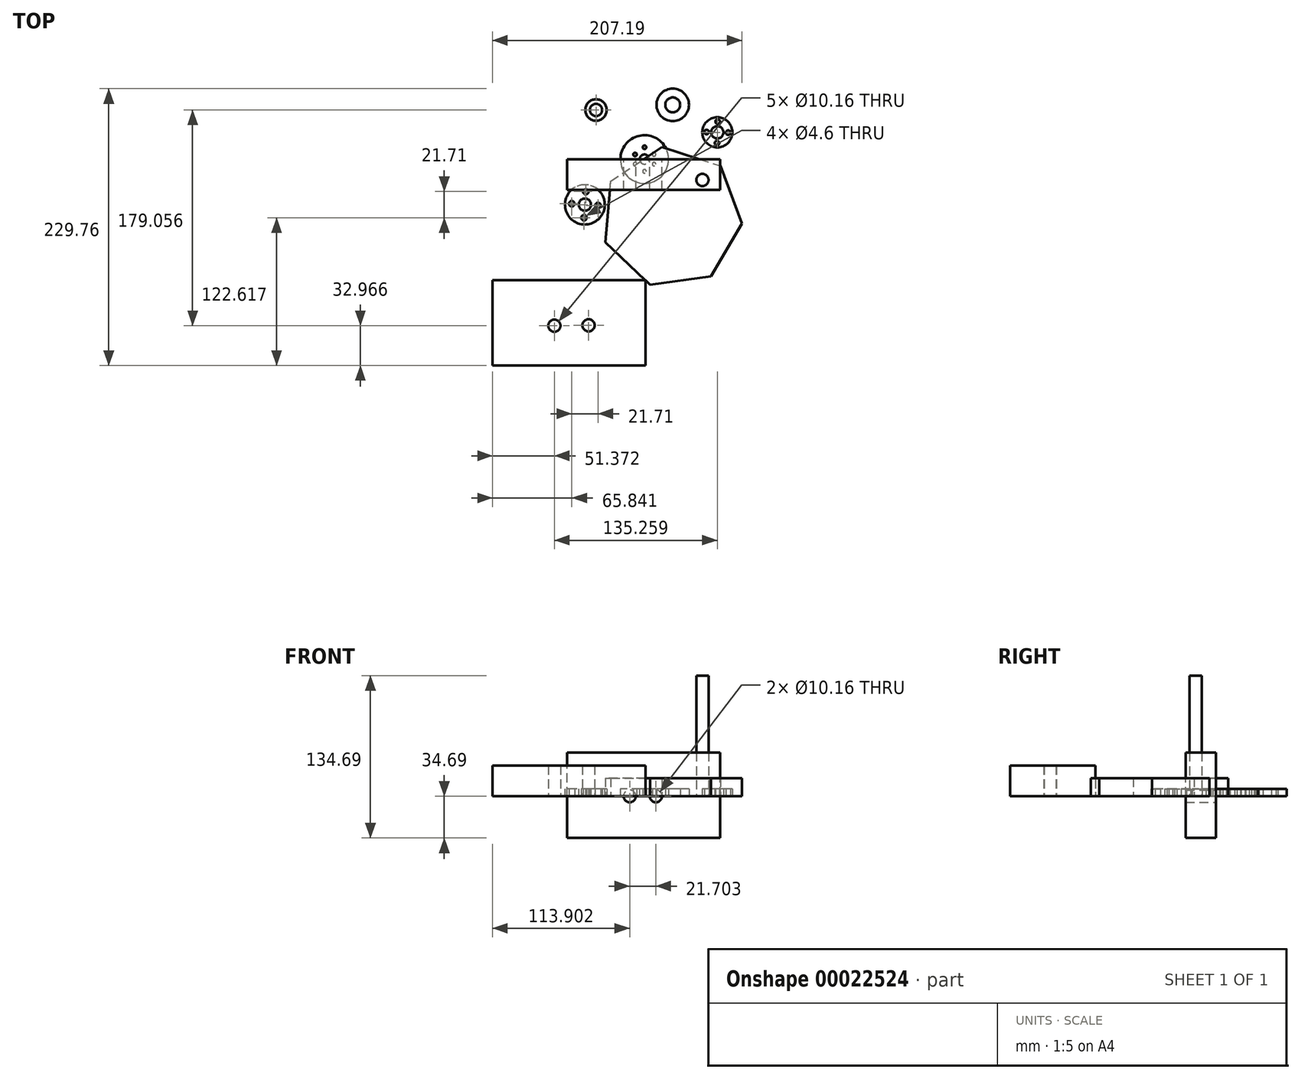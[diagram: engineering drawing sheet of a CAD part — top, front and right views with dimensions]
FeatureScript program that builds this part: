
annotation { "Feature Type Name" : "Feature", "Feature Type Description" : "" }
export const myFeature = defineFeature(function(context is Context, id is Id, definition is map)
    precondition{}
    {
        {
            var Q0;
            Q0=qCreatedBy(makeId("Top.planeOp"),FACE);
            var sketch = newSketch(context, id + "F0", { "sketchPlane" : qUnion([Q0])});
            skArc(sketch, "E0", {"start": v(20, 0) * mm, "mid": v(0, 20) * mm, "end": v(-20, 0) * mm});
            skLineSegment(sketch, "E1", {"start": v(-20, 0) * mm, "end": v(20, 0) * mm});
            skLineSegment(sketch, "E2", {"start": v(0, 20) * mm, "end": v(0, 0) * mm});
            skArc(sketch, "E3", {"start": v(4, 0) * mm, "mid": v(0, 4) * mm, "end": v(-4, 0) * mm});
            skLineSegment(sketch, "E4", {"start": v(-4, 0) * mm, "end": v(4, 0) * mm});
            skLineSegment(sketch, "E5", {"start": v(0, 4) * mm, "end": v(0, 10) * mm});
            skLineSegment(sketch, "E6", {"start": v(3.26, 2.32) * mm, "end": v(7.95, 4.06) * mm});
            skLineSegment(sketch, "E7", {"start": v(-3.05, 2.6) * mm, "end": v(-7.83, 4.06) * mm});
            skCircle(sketch, "E8", {"center": v(0, 10) * mm, "radius": 1.5 * mm});
            skCircle(sketch, "E9", {"center": v(7.95, 4.06) * mm, "radius": 1.5 * mm});
            skCircle(sketch, "E10", {"center": v(-7.83, 4.06) * mm, "radius": 1.5 * mm});
            skSolve(sketch);
        }
        {
            var Q0;
            Q0 = qSketchRegion(id + "F0", true);
            extrude(context, id + "F1", {"entities" : qUnion([Q0]), "depth" : 6 * mm});
        }
        {
            var Q0;
            Q0=makeQuery(id+"F1.opExtrude","SWEPT_BODY",BODY,{"disambiguationData":[OSD([sQuery(id+"F0.wireOp",EDGE,"E0"),sQuery(id+"F0.wireOp",EDGE,"E1"),sQuery(id+"F0.wireOp",EDGE,"E4"),sQuery(id+"F0.wireOp",EDGE,"E8"),sQuery(id+"F0.wireOp",EDGE,"E9"),sQuery(id+"F0.wireOp",EDGE,"E10")])]});
            var Q1;
            Q1=makeQuery(id+"F1.opExtrude","SWEPT_FACE",FACE,{"disambiguationData":[OSD([sQuery(id+"F0.wireOp",EDGE,"E1"),sQuery(id+"F0.wireOp",EDGE,"E4")])]});
            mirror(context, id + "F2", {"operationType" : NewBodyOperationType.ADD, "entities" : qUnion([Q0]), "mirrorPlane" : qUnion([Q1])});
        }
        {
            var Q0;
            {var subQ0=makeQuery(id+"F1.opExtrude","CAP_FACE",FACE,{"disambiguationData":[OSD([sQuery(id+"F0.wireOp",EDGE,"E0"),sQuery(id+"F0.wireOp",EDGE,"E1"),sQuery(id+"F0.wireOp",EDGE,"E4"),sQuery(id+"F0.wireOp",EDGE,"E8"),sQuery(id+"F0.wireOp",EDGE,"E9"),sQuery(id+"F0.wireOp",EDGE,"E10")])],"isStart":false});Q0=makeQuery(id+"F2.boolean.opBoolean","MERGE",FACE,{"derivedFrom":[subQ0,makeQuery(id+"F2.opPattern","COPY",FACE,{"derivedFrom":subQ0,"instanceName":"1"})]});}
            var sketch = newSketch(context, id + "F3", { "sketchPlane" : qUnion([Q0])});
            skCircle(sketch, "E11", {"center": v(0, 0) * mm, "radius": 4 * mm});
            skCircle(sketch, "E12", {"center": v(0, 0) * mm, "radius": 1.5 * mm});
            skCircle(sketch, "E13", {"center": v(0, 0) * mm, "radius": 16.5 * mm});
            skSolve(sketch);
        }
        {
            var Q0;
            Q0=makeQuery(id+"F3.imprint","IMPRINT",FACE,{"disambiguationData":[TD([[makeQuery(id+"F3.imprint","IMPRINT",EDGE,{"derivedFrom":sQuery(id+"F3.wireOp",EDGE,"E11")}),1.0]])]});
            extrude(context, id + "F4", {"entities" : qUnion([Q0]), "operationType" : NewBodyOperationType.ADD, "depth" : 1.5 * mm});
        }
        {
            var Q0;
            {var subQ0=makeQuery(id+"F1.opExtrude","CAP_FACE",FACE,{"disambiguationData":[OSD([sQuery(id+"F0.wireOp",EDGE,"E0"),sQuery(id+"F0.wireOp",EDGE,"E1"),sQuery(id+"F0.wireOp",EDGE,"E4"),sQuery(id+"F0.wireOp",EDGE,"E8"),sQuery(id+"F0.wireOp",EDGE,"E9"),sQuery(id+"F0.wireOp",EDGE,"E10")])],"isStart":false});Q0=makeQuery(id+"F4.boolean.opBoolean","SPLIT",FACE,{"disambiguationData":[TD([makeQuery(id+"F4.opExtrude","SWEPT_FACE",FACE,{"disambiguationData":[OSD([sQuery(id+"F3.wireOp",EDGE,"E12")])]})])],"derivedFrom":makeQuery(id+"F2.boolean.opBoolean","MERGE",FACE,{"derivedFrom":[subQ0,makeQuery(id+"F2.opPattern","COPY",FACE,{"derivedFrom":subQ0,"instanceName":"1"})]})});}
            extrude(context, id + "F5", {"entities" : qUnion([Q0]), "operationType" : NewBodyOperationType.REMOVE, "oppositeDirection" : true, "depth" : 141.56 * mm});
        }
        {
            var Q0;
            Q0=qCreatedBy(makeId("Top.planeOp"),FACE);
            var sketch = newSketch(context, id + "F6", { "sketchPlane" : qUnion([Q0])});
            skCircle(sketch, "E14", {"center": v(-40.22, 40.93) * mm, "radius": 8.9 * mm});
            skCircle(sketch, "E15", {"center": v(-40.22, 40.93) * mm, "radius": 5.08 * mm});
            skSolve(sketch);
        }
        {
            var Q0;
            Q0=makeQuery(id+"F6.imprint","IMPRINT",FACE,{"disambiguationData":[TD([[makeQuery(id+"F6.imprint","IMPRINT",EDGE,{"derivedFrom":sQuery(id+"F6.wireOp",EDGE,"E14")}),1.0]])]});
            extrude(context, id + "F7", {"entities" : qUnion([Q0]), "depth" : 6 * mm});
        }
        {
            var Q0;
            Q0=qCreatedBy(makeId("Top.planeOp"),FACE);
            var sketch = newSketch(context, id + "F8", { "sketchPlane" : qUnion([Q0])});
            skCircle(sketch, "E16", {"center": v(60.47, 22.4) * mm, "radius": 12.5 * mm});
            skCircle(sketch, "E17", {"center": v(60.47, 22.4) * mm, "radius": 5.08 * mm});
            skCircle(sketch, "E18", {"center": v(60.76, 31.33) * mm, "radius": 1.91 * mm});
            skCircle(sketch, "E19.1.0", {"center": v(51.53, 22.68) * mm, "radius": 1.91 * mm});
            skCircle(sketch, "E19.2.0", {"center": v(60.19, 13.45) * mm, "radius": 1.91 * mm});
            skCircle(sketch, "E19.3.0", {"center": v(69.41, 22.1) * mm, "radius": 1.91 * mm});
            skSolve(sketch);
        }
        {
            var Q0;
            Q0 = qSketchRegion(id + "F8", true);
            extrude(context, id + "F9", {"entities" : qUnion([Q0]), "depth" : 6 * mm});
        }
        {
            var Q0;
            Q0=qCreatedBy(makeId("Top.planeOp"),FACE);
            var sketch = newSketch(context, id + "F10", { "sketchPlane" : qUnion([Q0])});
            skCircle(sketch, "E20", {"center": v(-49.46, -37.62) * mm, "radius": 16.51 * mm});
            skCircle(sketch, "E21", {"center": v(-49.46, -37.62) * mm, "radius": 4.15 * mm});
            skCircle(sketch, "E22", {"center": v(-48.72, -26.76) * mm, "radius": 2.3 * mm});
            skCircle(sketch, "E23.1.0", {"center": v(-60.32, -36.87) * mm, "radius": 2.3 * mm});
            skCircle(sketch, "E23.2.0", {"center": v(-50.21, -48.47) * mm, "radius": 2.3 * mm});
            skCircle(sketch, "E23.3.0", {"center": v(-38.6, -38.36) * mm, "radius": 2.3 * mm});
            skCircle(sketch, "E24", {"center": v(-49.46, -37.62) * mm, "radius": 5.08 * mm});
            skLineSegment(sketch, "E25", {"start": v(-46.78, -33.3) * mm, "end": v(-52.08, -41.97) * mm});
            skCircle(sketch, "E26", {"center": v(23.44, 45.19) * mm, "radius": 6.18 * mm});
            skLineSegment(sketch, "E27", {"start": v(23.44, 51.37) * mm, "end": v(23.44, 39) * mm});
            skCircle(sketch, "E28", {"center": v(23.44, 45.19) * mm, "radius": 13.49 * mm});
            skSolve(sketch);
        }
        {
            var Q0;
            Q0=makeQuery(id+"F10.imprint","IMPRINT",FACE,{"disambiguationData":[TD([[makeQuery(id+"F10.imprint","IMPRINT",EDGE,{"derivedFrom":sQuery(id+"F10.wireOp",EDGE,"E20")}),1.0]])]});
            extrude(context, id + "F11", {"entities" : qUnion([Q0]), "depth" : 6 * mm});
        }
        {
            var Q0;
            Q0=makeQuery(id+"F4.opExtrude","CAP_FACE",FACE,{"disambiguationData":[OSD([sQuery(id+"F3.wireOp",EDGE,"E11"),sQuery(id+"F3.wireOp",EDGE,"E12")])],"isStart":false});
            extrude(context, id + "F12", {"entities" : qUnion([Q0]), "operationType" : NewBodyOperationType.REMOVE, "oppositeDirection" : true, "depth" : 254 * mm});
        }
        {
            var Q0;
            Q0=makeQuery(id+"F10.imprint","IMPRINT",FACE,{"disambiguationData":[TD([[makeQuery(id+"F10.imprint","IMPRINT",EDGE,{"derivedFrom":sQuery(id+"F10.wireOp",EDGE,"E28")}),1.0]])]});
            extrude(context, id + "F13", {"entities" : qUnion([Q0]), "depth" : 6 * mm});
        }
        {
            var Q0;
            Q0=qCreatedBy(makeId("Top.planeOp"),FACE);
            var sketch = newSketch(context, id + "F14", { "sketchPlane" : qUnion([Q0])});
            skCircle(sketch, "E29.cCircle", {"center": v(22.54, -48.1) * mm, "radius": 52.9 * mm, "construction": true});
            skLineSegment(sketch, "E29.0", {"start": v(4.58, -103.99) * mm, "end": v(-32.36, -68.9) * mm});
            skLineSegment(sketch, "E29.1", {"start": v(-32.36, -68.9) * mm, "end": v(-27.95, -18.15) * mm});
            skLineSegment(sketch, "E29.2", {"start": v(-27.95, -18.15) * mm, "end": v(14.48, 10.05) * mm});
            skLineSegment(sketch, "E29.3", {"start": v(14.48, 10.05) * mm, "end": v(62.98, -5.54) * mm});
            skLineSegment(sketch, "E29.4", {"start": v(62.98, -5.54) * mm, "end": v(81.03, -53.17) * mm});
            skLineSegment(sketch, "E29.5", {"start": v(81.03, -53.17) * mm, "end": v(55.04, -97) * mm});
            skLineSegment(sketch, "E29.6", {"start": v(55.04, -97) * mm, "end": v(4.58, -103.99) * mm});
            skPoint(sketch, "E29.0.midPoint", {"position": v(-13.89, -86.45) * mm});
            skSolve(sketch);
        }
        {
            var Q0;
            Q0=makeQuery(id+"F14.imprint","IMPRINT",FACE,{"disambiguationData":[TD([[makeQuery(id+"F14.imprint","IMPRINT",EDGE,{"derivedFrom":sQuery(id+"F14.wireOp",EDGE,"E29.0")}),-1.0]])]});
            extrude(context, id + "F15", {"entities" : qUnion([Q0]), "depth" : 15 * mm});
        }
        {
            var Q0;
            Q0=qCreatedBy(makeId("Top.planeOp"),FACE);
            var sketch = newSketch(context, id + "F16", { "sketchPlane" : qUnion([Q0])});
            skCircle(sketch, "E30", {"center": v(48.08, -17.13) * mm, "radius": 5.08 * mm});
            skSolve(sketch);
        }
        {
            var Q0;
            Q0=makeQuery(id+"F16.imprint","IMPRINT",FACE,{"disambiguationData":[TD([[makeQuery(id+"F16.imprint","IMPRINT",EDGE,{"derivedFrom":sQuery(id+"F16.wireOp",EDGE,"E30")}),1.0]])]});
            extrude(context, id + "F17", {"entities" : qUnion([Q0]), "depth" : 100 * mm});
        }
        {
            var Q0;
            Q0=makeQuery(id+"F15.opExtrude","CAP_FACE",FACE,{"disambiguationData":[OSD([sQuery(id+"F14.wireOp",EDGE,"E29.0"),sQuery(id+"F14.wireOp",EDGE,"E29.1"),sQuery(id+"F14.wireOp",EDGE,"E29.2"),sQuery(id+"F14.wireOp",EDGE,"E29.3"),sQuery(id+"F14.wireOp",EDGE,"E29.4"),sQuery(id+"F14.wireOp",EDGE,"E29.5"),sQuery(id+"F14.wireOp",EDGE,"E29.6")])],"isStart":false});
            var sketch = newSketch(context, id + "F18", { "sketchPlane" : qUnion([Q0])});
            skLineSegment(sketch, "E31", {"start": v(55.04, -97) * mm, "end": v(-6.74, -4.05) * mm});
            skLineSegment(sketch, "E32", {"start": v(62.98, -5.54) * mm, "end": v(-14.81, -85.57) * mm});
            skLineSegment(sketch, "E33", {"start": v(-14.81, -85.57) * mm, "end": v(62.98, -5.54) * mm});
            skLineSegment(sketch, "E34", {"start": v(81.03, -53.17) * mm, "end": v(-30.15, -43.52) * mm});
            skCircle(sketch, "E35", {"center": v(22.16, -47.53) * mm, "radius": 6.18 * mm});
            skCircle(sketch, "E36", {"center": v(0, -46.14) * mm, "radius": 7.62 * mm});
            skCircle(sketch, "E37", {"center": v(52.57, -50.7) * mm, "radius": 7.62 * mm});
            skSolve(sketch);
        }
        {
            var Q0;
            Q0=qCreatedBy(makeId("Top.planeOp"),FACE);
            var sketch = newSketch(context, id + "F19", { "sketchPlane" : qUnion([Q0])});
            skLineSegment(sketch, "E38.bottom", {"start": v(-126.16, -171.1) * mm, "end": v(0.84, -171.1) * mm});
            skLineSegment(sketch, "E38.top", {"start": v(-126.16, -100.17) * mm, "end": v(0.84, -100.17) * mm});
            skLineSegment(sketch, "E38.left", {"start": v(-126.16, -171.1) * mm, "end": v(-126.16, -100.17) * mm});
            skLineSegment(sketch, "E38.right", {"start": v(0.84, -171.1) * mm, "end": v(0.84, -100.17) * mm});
            skCircle(sketch, "E39", {"center": v(-46.39, -137.78) * mm, "radius": 5.08 * mm});
            skCircle(sketch, "E40", {"center": v(-74.79, -138.12) * mm, "radius": 5.08 * mm});
            skSolve(sketch);
        }
        {
            var Q0;
            Q0 = qSketchRegion(id + "F19", true);
            extrude(context, id + "F20", {"entities" : qUnion([Q0]), "depth" : 25.4 * mm});
        }
        {
            var Q0;
            Q0=qCreatedBy(makeId("Front.planeOp"),FACE);
            var sketch = newSketch(context, id + "F21", { "sketchPlane" : qUnion([Q0])});
            skLineSegment(sketch, "E41.bottom", {"start": v(-64.2, -34.69) * mm, "end": v(62.8, -34.69) * mm});
            skLineSegment(sketch, "E41.top", {"start": v(-64.2, 36.24) * mm, "end": v(62.8, 36.24) * mm});
            skLineSegment(sketch, "E41.left", {"start": v(-64.2, -34.69) * mm, "end": v(-64.2, 36.24) * mm});
            skLineSegment(sketch, "E41.right", {"start": v(62.8, -34.69) * mm, "end": v(62.8, 36.24) * mm});
            skCircle(sketch, "E42", {"center": v(9.44, 0) * mm, "radius": 5.08 * mm});
            skCircle(sketch, "E43", {"center": v(-12.26, 0) * mm, "radius": 5.08 * mm});
            skSolve(sketch);
        }
        {
            var Q0;
            Q0=makeQuery(id+"F21.imprint","IMPRINT",FACE,{"disambiguationData":[TD([[makeQuery(id+"F21.imprint","IMPRINT",EDGE,{"derivedFrom":sQuery(id+"F21.wireOp",EDGE,"E41.bottom")}),1.0]])]});
            extrude(context, id + "F22", {"entities" : qUnion([Q0]), "depth" : 25.4 * mm});
        }
    });
